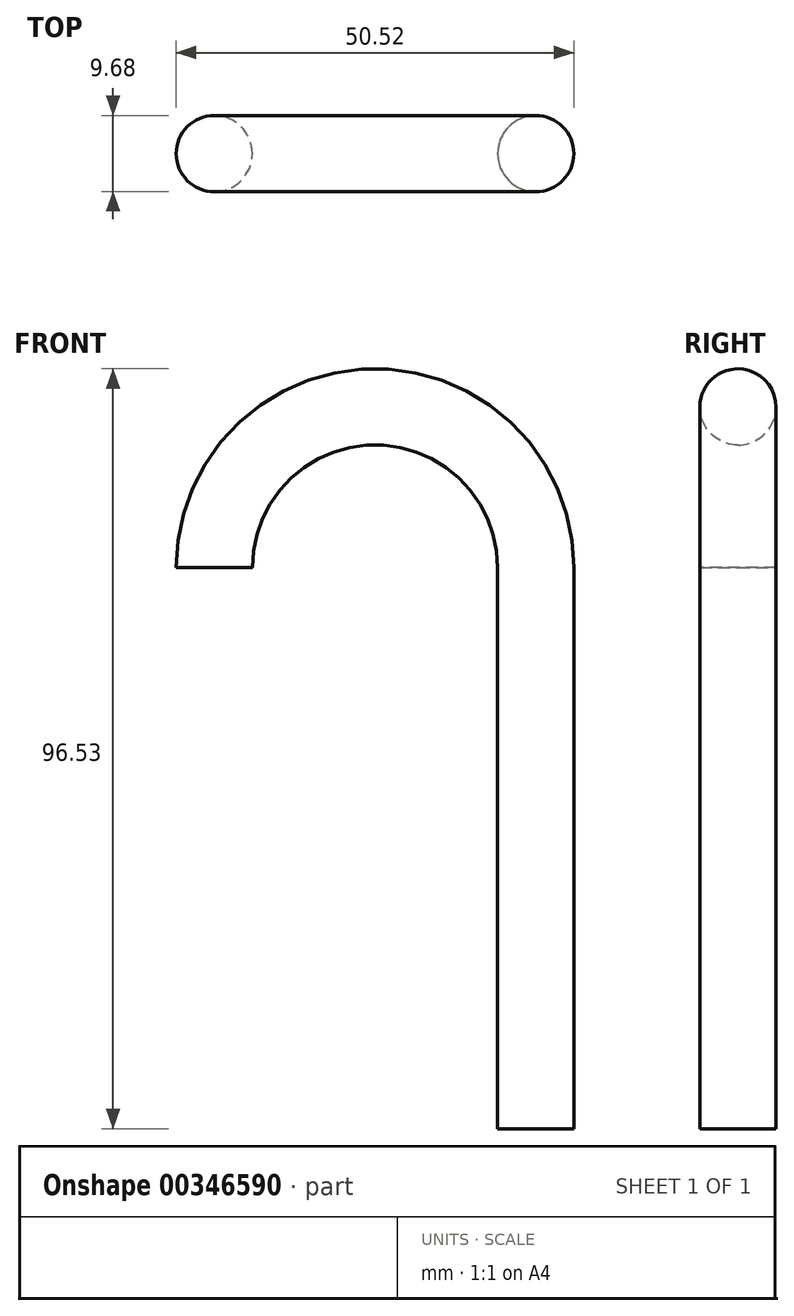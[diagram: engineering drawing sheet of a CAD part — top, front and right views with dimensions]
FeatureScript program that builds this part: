
annotation { "Feature Type Name" : "Feature", "Feature Type Description" : "" }
export const myFeature = defineFeature(function(context is Context, id is Id, definition is map)
    precondition{}
    {
        {
            var Q0;
            Q0=qCreatedBy(makeId("Front.planeOp"),FACE);
            var sketch = newSketch(context, id + "F0", { "sketchPlane" : qUnion([Q0])});
            skLineSegment(sketch, "E0", {"start": v(0, 0) * mm, "end": v(0, -71.27) * mm});
            skArc(sketch, "E1", {"start": v(0, 0) * mm, "mid": v(-20.4, 20.4) * mm, "end": v(-40.8, 0) * mm});
            skSolve(sketch);
        }
        {
            var Q0;
            Q0=qCreatedBy(makeId("Top.planeOp"),FACE);
            var sketch = newSketch(context, id + "F1", { "sketchPlane" : qUnion([Q0])});
            skCircle(sketch, "E2", {"center": v(-40.83, 0) * mm, "radius": 4.84 * mm});
            skSolve(sketch);
        }
        {
            var Q0;
            Q0=makeQuery(id+"F1.imprint","IMPRINT",FACE,{"disambiguationData":[TD([[makeQuery(id+"F1.imprint","IMPRINT",EDGE,{"derivedFrom":sQuery(id+"F1.wireOp",EDGE,"E2")}),1.0]])]});
            var Q1;
            Q1=sQuery(id+"F0.wireOp",EDGE,"E1");
            var Q2;
            Q2=sQuery(id+"F0.wireOp",EDGE,"E0");
            sweep(context, id + "F2", {"profiles" : qUnion([Q0]), "path" : qUnion([Q1, Q2])});
        }
        {
            var Q0;
            Q0=qCreatedBy(makeId("Front.planeOp"),FACE);
            cPlane(context, id + "F3", {"entities" : qUnion([Q0]), "cplaneType" : CPlaneType.OFFSET, "offset" : 9.4 * mm, "width" : 152.4 * mm, "height" : 152.4 * mm});
        }
    });
